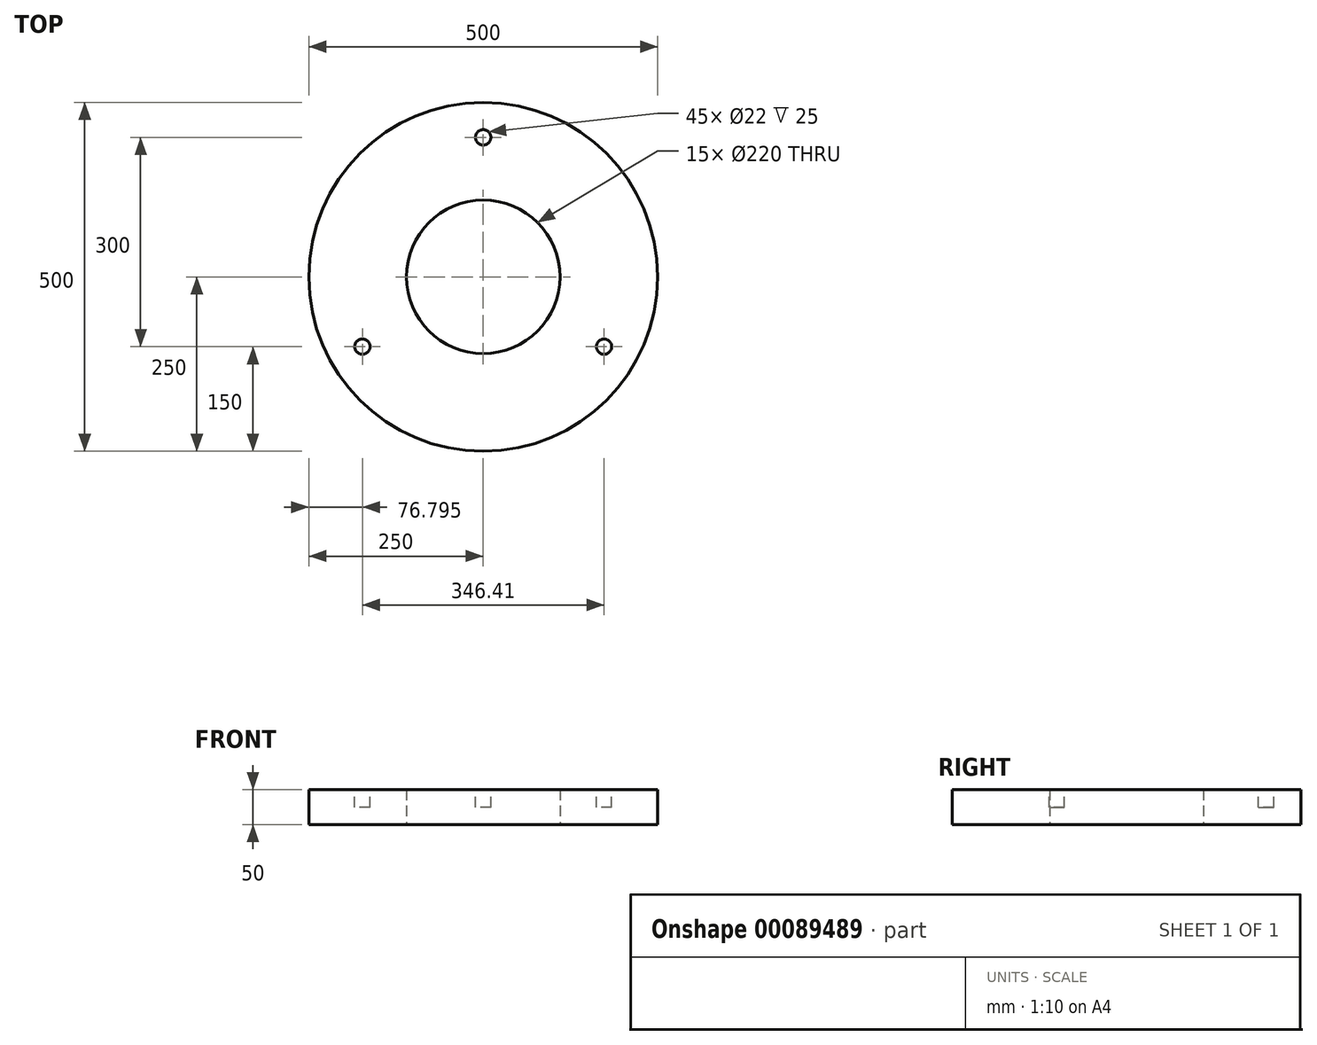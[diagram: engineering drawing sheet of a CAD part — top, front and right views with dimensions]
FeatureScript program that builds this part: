
annotation { "Feature Type Name" : "Feature", "Feature Type Description" : "" }
export const myFeature = defineFeature(function(context is Context, id is Id, definition is map)
    precondition{}
    {
        {
            var Q0;
            Q0=qCreatedBy(makeId("Top.planeOp"),FACE);
            var sketch = newSketch(context, id + "F0", { "sketchPlane" : qUnion([Q0])});
            skCircle(sketch, "E0", {"center": v(0, 0) * mm, "radius": 250 * mm});
            skCircle(sketch, "E1", {"center": v(0, 0) * mm, "radius": 110 * mm});
            skSolve(sketch);
        }
        {
            var Q0;
            Q0 = qSketchRegion(id + "F0", true);
            extrude(context, id + "F1", {"entities" : qUnion([Q0]), "depth" : 50 * mm});
        }
        {
            var Q0;
            Q0=makeQuery(id+"F1.opExtrude","CAP_FACE",FACE,{"disambiguationData":[OSD([sQuery(id+"F0.wireOp",EDGE,"E0"),sQuery(id+"F0.wireOp",EDGE,"E1")])],"isStart":false});
            var sketch = newSketch(context, id + "F2", { "sketchPlane" : qUnion([Q0])});
            skCircle(sketch, "E2", {"center": v(0, 0) * mm, "radius": 200 * mm, "construction": true});
            skCircle(sketch, "E3", {"center": v(0, 200) * mm, "radius": 11 * mm});
            skCircle(sketch, "E4.1.0", {"center": v(-173.2, -100) * mm, "radius": 11 * mm});
            skCircle(sketch, "E4.2.0", {"center": v(173.2, -100) * mm, "radius": 11 * mm});
            skSolve(sketch);
        }
        {
            var Q0;
            Q0 = qSketchRegion(id + "F2", true);
            extrude(context, id + "F3", {"entities" : qUnion([Q0]), "operationType" : NewBodyOperationType.REMOVE, "oppositeDirection" : true, "depth" : 25 * mm});
        }
    });
